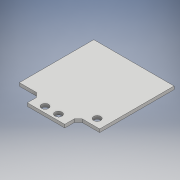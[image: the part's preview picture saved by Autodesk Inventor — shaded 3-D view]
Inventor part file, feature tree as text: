
AUTODESK INVENTOR PART (.ipt)
format: ipt  version: 2017 (Build 210142000, 142)  size: 115,712 bytes
history: native  units: mm
features: other x1, extrude x1, chamfer x1, sketch x1
ambient origin geometry x8: Origin, YZ Plane, XZ Plane, XY Plane, X Axis, Y Axis, Z Axis, Center Point
bodies: Body1 (feature_tree)
feature tree (4):
  other  "ソリッド1"
  extrude  "押し出し1"  Depth=3.4mm
  chamfer  "面取り1"  Distance=17.8mm
  sketch  "スケッチ1"
